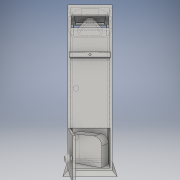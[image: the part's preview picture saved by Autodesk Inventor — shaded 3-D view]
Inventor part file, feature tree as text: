
AUTODESK INVENTOR PART (.ipt)
format: ipt  version: 2016 (Build 200138000, 138)  size: 381,952 bytes
history: native  units: in
note: dims shown in document units (in); Inventor stores cm internally (conversion verified against a paired STEP export)
features: sketch x23, extrude x21, fillet x2, chamfer x1, plane x1, loft x1
ambient origin geometry x8: Origin, YZ Plane, XZ Plane, XY Plane, X Axis, Y Axis, Z Axis, Center Point
bodies: Solid1 (feature_tree)
feature tree (49):
  extrude  "Extrusion1"  Depth=16.0in TaperAngle=0.0deg
  extrude  "Extrusion2"  Depth=2.0in TaperAngle=0.0deg
  extrude  "Extrusion3"  Depth=18.0in TaperAngle=0.0deg
  extrude  "Extrusion4"  Depth=2.0in
  chamfer  "Chamfer1"  Angle=90.0deg  [1 undecoded]
  sketch  "Sketch5"  dims[d33=6.5in]
  plane  "Work Plane1"
  loft  "Loft1"
  extrude  "Extrusion5"  Depth=2.56in TaperAngle=0.0deg
  extrude  "Extrusion6"  Depth=0.94in
  extrude  "Extrusion7"  Depth=1.5in
  extrude  "Extrusion8"  Depth=1.5in
  extrude  "Extrusion9"  Depth=5.5in TaperAngle=0.0deg
  extrude  "Extrusion10"  Depth=1.25in
  extrude  "Extrusion11"  Depth=1.25in
  extrude  "Extrusion12"  Depth=1.25in
  fillet  "Fillet1"  Radius=1.0in
  extrude  "Extrusion13"  Depth=18.0in
  extrude  "Extrusion14"  Depth=1.0in
  extrude  "Extrusion15"  Depth=1.0in
  extrude  "Extrusion16"  Depth=2.8in TaperAngle=0.0deg
  extrude  "Extrusion17"  Depth=16.0in TaperAngle=0.0deg
  extrude  "Extrusion18"  Depth=16.5in
  extrude  "Extrusion19"  Depth=4.125in
  fillet  "Fillet2"  Radius=12.0in
  extrude  "Extrusion20"  Depth=2.8in
  extrude  "Extrusion21"  Depth=1.0in
  sketch  "Sketch1"  dims[d0=64.0in d1=20.0in d3=1.0in d4=1.0in d5=1.0in d6=1.0in d7=2.0in d8=2.0in d19=2.0in d20=16.0in d21=0.0in]
  sketch  "Sketch2"  dims[d22=2.0in d23=0.0in d24=2.0in d25=0.0in]
  sketch  "Sketch3"  dims[d26=1.0in d27=18.0in d28=0.0in]
  sketch  "Sketch4"  dims[d29=2.0in d30=0.125in d31=45.0deg d32=11.75in]
  sketch  "Sketch6"  dims[d34=2.5in d35=0.0in d36=90.0deg]
  sketch  "Sketch7"  dims[d37=0.0in d38=90.0deg d39=13.3in]
  sketch  "Sketch8"  dims[d40=16.2in d41=2.56in d42=0.0in]
  sketch  "Sketch9"  dims[d49=8.1in d50=0.94in]
  sketch  "Sketch10"  dims[d51=25.565in d52=0.0in d53=1.5in]
  sketch  "Sketch11"  dims[d54=1.5in d55=1.5in]
  sketch  "Sketch12"  dims[d56=1.5in d57=5.5in d58=0.0in]
  sketch  "Sketch13"  dims[d59=1.25in d60=1.25in]
  sketch  "Sketch14"  dims[d61=1.25in d62=1.25in]
  sketch  "Sketch16"  dims[d63=1.25in d64=1.25in d65=1.0in d66=0.0in]
  sketch  "Sketch17"  dims[d67=1.0in d68=18.0in]
  sketch  "Sketch18"  dims[d69=18.0in d70=0.0in d71=1.0in]
  sketch  "Sketch19"  dims[d72=1.0in d73=1.0in]
  sketch  "Sketch20"  dims[d74=1.0in d76=2.8in d77=0.0in]
  sketch  "Sketch21"  dims[d78=1.0in d79=16.0in d80=0.0in]
  sketch  "Sketch22"  dims[d81=6.75in d82=16.5in]
  sketch  "Sketch23"  dims[d83=14.0in d84=0.0in d85=4.125in d95=12.0in]
  sketch  "Sketch24"  dims[d96=3.0in d99=2.8in d100=37.0in d101=1.625in d102=0.0in d104=2.5in d105=3.875in d106=0.0in d107=0.5in d108=10.5in d109=0.0in d111=0.5in d112=0.0in d113=18.0in d114=11.0in d115=0.5in d116=18.0in d117=1.0in d118=18.0in d119=0.0in d120=1.5in d121=0.75in d122=0.0in d123=4.0in d124=2.0in d125=0.0in d126=1.0in d127=3.0in d128=0.0in d129=0.5in d130=1.8in d131=0.0in d132=1.0in d133=1.3125in d134=0.0in d135=2.0in d86=1.0in d87=1.0in]
note: 1 required parameter value undecoded (feature->parameter linkage not recoverable at this tier; creation-order binding heuristic only, values carry confidence <= 0.55)
